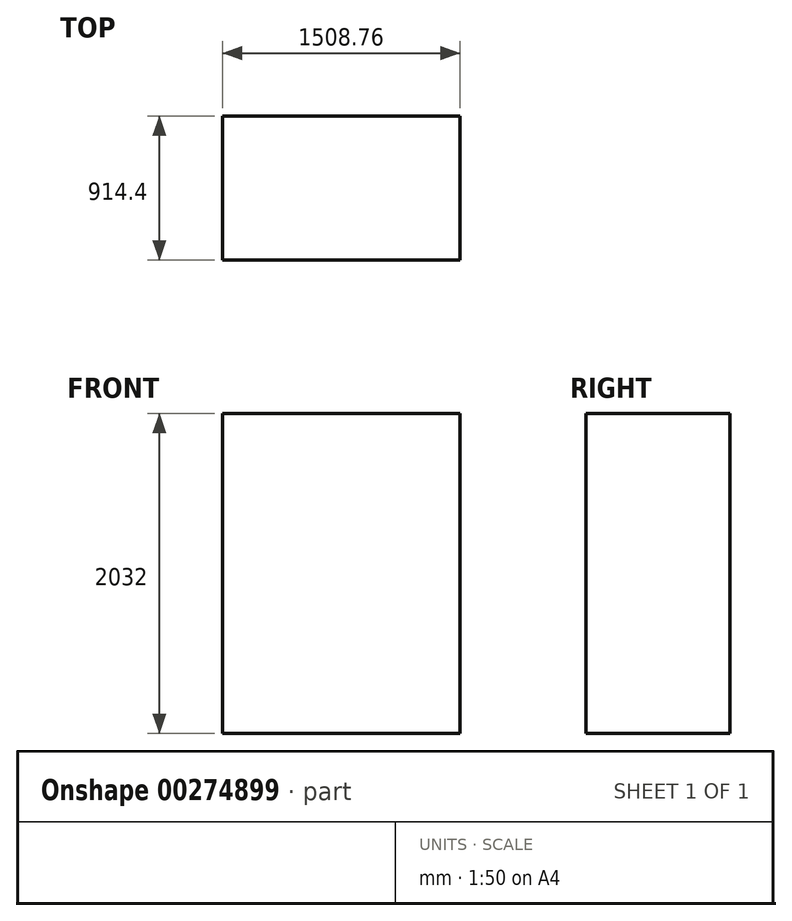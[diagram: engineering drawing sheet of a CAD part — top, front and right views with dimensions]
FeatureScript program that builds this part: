
annotation { "Feature Type Name" : "Feature", "Feature Type Description" : "" }
export const myFeature = defineFeature(function(context is Context, id is Id, definition is map)
    precondition{}
    {
        {
            var Q0;
            Q0=qCreatedBy(makeId("Top.planeOp"),FACE);
            var sketch = newSketch(context, id + "F0", { "sketchPlane" : qUnion([Q0])});
            skLineSegment(sketch, "E0.bottom", {"start": v(0, 0) * mm, "end": v(1066.8, 0) * mm});
            skLineSegment(sketch, "E0.top", {"start": v(0, 914.4) * mm, "end": v(1066.8, 914.4) * mm});
            skLineSegment(sketch, "E0.left", {"start": v(0, 0) * mm, "end": v(0, 914.4) * mm});
            skLineSegment(sketch, "E0.right", {"start": v(1066.8, 0) * mm, "end": v(1066.8, 914.4) * mm});
            skSolve(sketch);
        }
        {
            var Q0;
            Q0=makeQuery(id+"F0.imprint","IMPRINT",FACE,{"disambiguationData":[TD([[makeQuery(id+"F0.imprint","IMPRINT",EDGE,{"derivedFrom":sQuery(id+"F0.wireOp",EDGE,"E0.bottom")}),1.0]])]});
            extrude(context, id + "F1", {"entities" : qUnion([Q0]), "depth" : 1778 * mm});
        }
        {
            var Q0;
            Q0=makeQuery(id+"F1.opExtrude","SWEPT_FACE",FACE,{"disambiguationData":[OSD([sQuery(id+"F0.wireOp",EDGE,"E0.left")])]});
            extrude(context, id + "F2", {"entities" : qUnion([Q0]), "operationType" : NewBodyOperationType.ADD, "depth" : 441.96 * mm});
        }
        {
            var Q0;
            {var subQ0=sQuery(id+"F0.wireOp",EDGE,"E0.left");Q0=makeQuery(id+"F2.boolean.opBoolean","MERGE",FACE,{"derivedFrom":[makeQuery(id+"F1.opExtrude","CAP_FACE",FACE,{"disambiguationData":[OSD([sQuery(id+"F0.wireOp",EDGE,"E0.bottom"),sQuery(id+"F0.wireOp",EDGE,"E0.top"),subQ0,sQuery(id+"F0.wireOp",EDGE,"E0.right")])],"isStart":false}),makeQuery(id+"F2.opExtrude","SWEPT_FACE",FACE,{"disambiguationData":[OSD([subQ0]),TDD([makeQuery(id+"F1.opExtrude","CAP_EDGE",EDGE,{"disambiguationData":[OSD([subQ0])],"isStart":false})])]})]});}
            extrude(context, id + "F3", {"entities" : qUnion([Q0]), "operationType" : NewBodyOperationType.REMOVE, "oppositeDirection" : true, "depth" : 355.6 * mm});
        }
        {
            var Q0;
            Q0=makeQuery(id+"F3.boolean.opBoolean","COPY",FACE,{"derivedFrom":makeQuery(id+"F3.opExtrude","CAP_FACE",FACE,{"disambiguationData":[OSD([sQuery(id+"F0.wireOp",EDGE,"E0.bottom"),sQuery(id+"F0.wireOp",EDGE,"E0.top"),sQuery(id+"F0.wireOp",EDGE,"E0.left"),sQuery(id+"F0.wireOp",EDGE,"E0.right")])],"isStart":false})});
            extrude(context, id + "F4", {"entities" : qUnion([Q0]), "operationType" : NewBodyOperationType.ADD, "depth" : 609.6 * mm, "offsetDistance" : 25.4 * mm});
        }
    });
